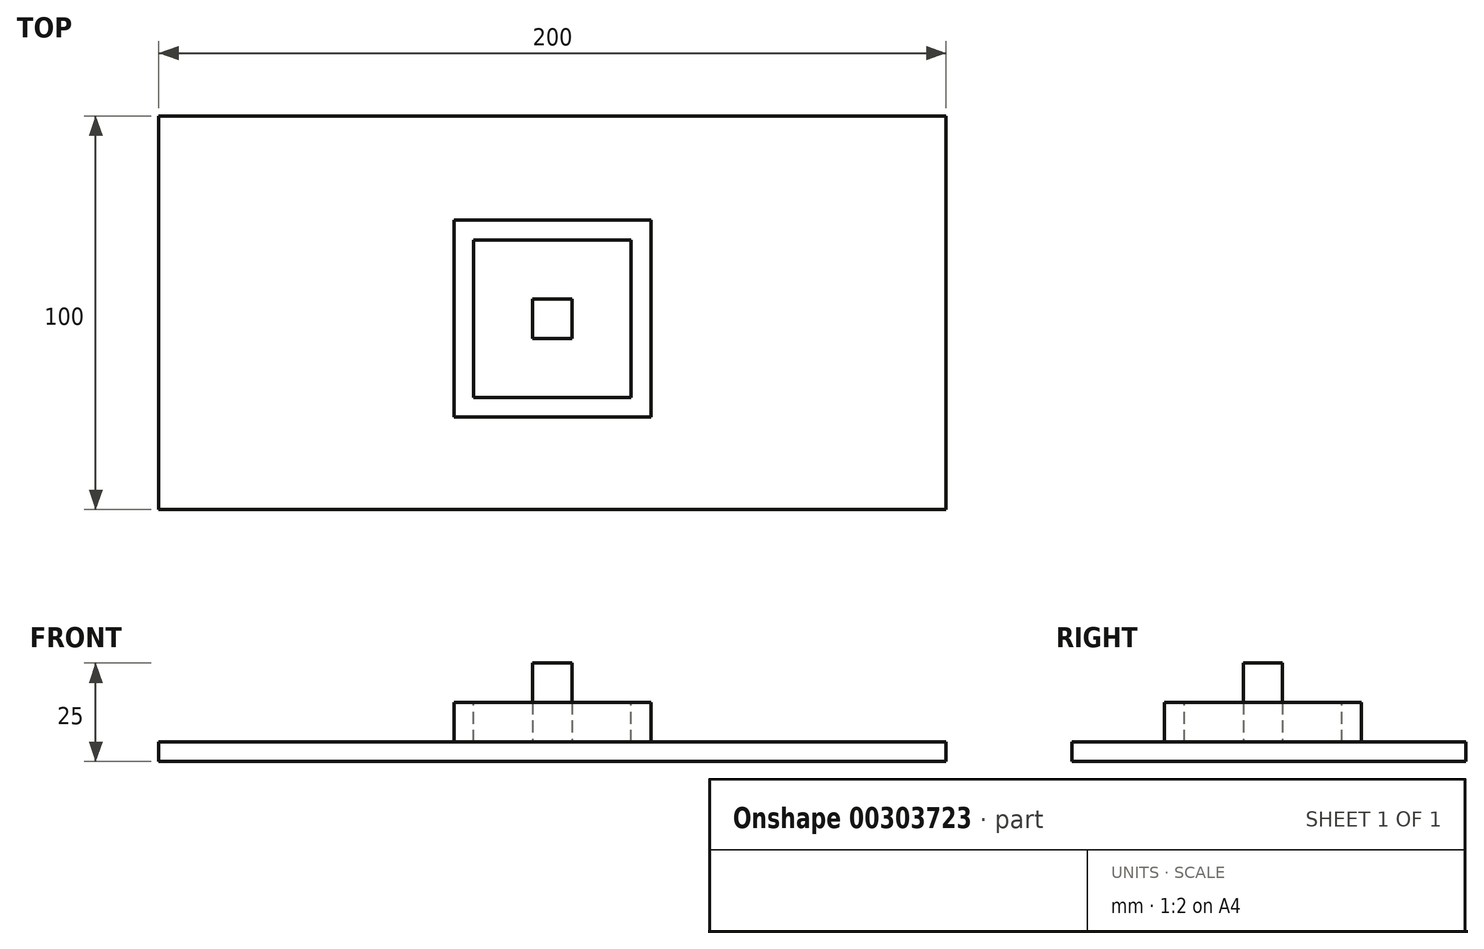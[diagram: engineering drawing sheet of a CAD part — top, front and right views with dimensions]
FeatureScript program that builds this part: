
annotation { "Feature Type Name" : "Feature", "Feature Type Description" : "" }
export const myFeature = defineFeature(function(context is Context, id is Id, definition is map)
    precondition{}
    {
        {
            var Q0;
            Q0=qCreatedBy(makeId("Top.planeOp"),FACE);
            var sketch = newSketch(context, id + "F0", { "sketchPlane" : qUnion([Q0])});
            skLineSegment(sketch, "E0.bottom", {"start": v(100, -48.5) * mm, "end": v(-100, -48.5) * mm});
            skLineSegment(sketch, "E0.top", {"start": v(100, 51.5) * mm, "end": v(-100, 51.5) * mm});
            skLineSegment(sketch, "E0.left", {"start": v(100, -48.5) * mm, "end": v(100, 51.5) * mm});
            skLineSegment(sketch, "E0.right", {"start": v(-100, -48.5) * mm, "end": v(-100, 51.5) * mm});
            skPoint(sketch, "E0.middle", {"position": v(0, 1.5) * mm});
            skSolve(sketch);
        }
        {
            var Q0;
            Q0=makeQuery(id+"F0.imprint","IMPRINT",FACE,{"disambiguationData":[TD([[makeQuery(id+"F0.imprint","IMPRINT",EDGE,{"derivedFrom":sQuery(id+"F0.wireOp",EDGE,"E0.bottom")}),-1.0]])]});
            extrude(context, id + "F1", {"entities" : qUnion([Q0]), "depth" : 5 * mm});
        }
        {
            var Q0;
            Q0=makeQuery(id+"F1.opExtrude","CAP_FACE",FACE,{"disambiguationData":[OSD([sQuery(id+"F0.wireOp",EDGE,"E0.bottom"),sQuery(id+"F0.wireOp",EDGE,"E0.top"),sQuery(id+"F0.wireOp",EDGE,"E0.left"),sQuery(id+"F0.wireOp",EDGE,"E0.right")])],"isStart":false});
            var sketch = newSketch(context, id + "F2", { "sketchPlane" : qUnion([Q0])});
            skLineSegment(sketch, "E1.bottom", {"start": v(25, -25) * mm, "end": v(-25, -25) * mm});
            skLineSegment(sketch, "E1.top", {"start": v(25, 25) * mm, "end": v(-25, 25) * mm});
            skLineSegment(sketch, "E1.left", {"start": v(25, -25) * mm, "end": v(25, 25) * mm});
            skLineSegment(sketch, "E1.right", {"start": v(-25, -25) * mm, "end": v(-25, 25) * mm});
            skPoint(sketch, "E1.middle", {"position": v(0, 0) * mm});
            skSolve(sketch);
        }
        {
            var Q0;
            Q0=makeQuery(id+"F2.imprint","IMPRINT",FACE,{"disambiguationData":[TD([[makeQuery(id+"F2.imprint","IMPRINT",EDGE,{"derivedFrom":sQuery(id+"F2.wireOp",EDGE,"E1.bottom")}),-1.0]])]});
            extrude(context, id + "F3", {"entities" : qUnion([Q0]), "operationType" : NewBodyOperationType.ADD, "depth" : 10 * mm});
        }
        {
            var Q0;
            Q0=makeQuery(id+"F3.opExtrude","CAP_FACE",FACE,{"disambiguationData":[OSD([sQuery(id+"F2.wireOp",EDGE,"E1.bottom"),sQuery(id+"F2.wireOp",EDGE,"E1.top"),sQuery(id+"F2.wireOp",EDGE,"E1.left"),sQuery(id+"F2.wireOp",EDGE,"E1.right")])],"isStart":false});
            var sketch = newSketch(context, id + "F4", { "sketchPlane" : qUnion([Q0])});
            skLineSegment(sketch, "E2.bottom", {"start": v(20, -20) * mm, "end": v(-20, -20) * mm});
            skLineSegment(sketch, "E2.top", {"start": v(20, 20) * mm, "end": v(-20, 20) * mm});
            skLineSegment(sketch, "E2.left", {"start": v(20, -20) * mm, "end": v(20, 20) * mm});
            skLineSegment(sketch, "E2.right", {"start": v(-20, -20) * mm, "end": v(-20, 20) * mm});
            skPoint(sketch, "E2.middle", {"position": v(0, 0) * mm});
            skSolve(sketch);
        }
        {
            var Q0;
            Q0=makeQuery(id+"F4.imprint","IMPRINT",FACE,{"disambiguationData":[TD([[makeQuery(id+"F4.imprint","IMPRINT",EDGE,{"derivedFrom":sQuery(id+"F4.wireOp",EDGE,"E2.bottom")}),-1.0]])]});
            extrude(context, id + "F5", {"entities" : qUnion([Q0]), "operationType" : NewBodyOperationType.REMOVE, "oppositeDirection" : true, "depth" : 10 * mm});
        }
        {
            var Q0;
            Q0=makeQuery(id+"F5.boolean.opBoolean","COPY",FACE,{"derivedFrom":makeQuery(id+"F5.opExtrude","CAP_FACE",FACE,{"disambiguationData":[OSD([sQuery(id+"F4.wireOp",EDGE,"E2.bottom"),sQuery(id+"F4.wireOp",EDGE,"E2.top"),sQuery(id+"F4.wireOp",EDGE,"E2.left"),sQuery(id+"F4.wireOp",EDGE,"E2.right")])],"isStart":false})});
            var sketch = newSketch(context, id + "F6", { "sketchPlane" : qUnion([Q0])});
            skLineSegment(sketch, "E3.bottom", {"start": v(5, -5) * mm, "end": v(-5, -5) * mm});
            skLineSegment(sketch, "E3.top", {"start": v(5, 5) * mm, "end": v(-5, 5) * mm});
            skLineSegment(sketch, "E3.left", {"start": v(5, -5) * mm, "end": v(5, 5) * mm});
            skLineSegment(sketch, "E3.right", {"start": v(-5, -5) * mm, "end": v(-5, 5) * mm});
            skPoint(sketch, "E3.middle", {"position": v(0, 0) * mm});
            skSolve(sketch);
        }
        {
            var Q0;
            Q0=makeQuery(id+"F6.imprint","IMPRINT",FACE,{"disambiguationData":[TD([[makeQuery(id+"F6.imprint","IMPRINT",EDGE,{"derivedFrom":sQuery(id+"F6.wireOp",EDGE,"E3.bottom")}),-1.0]])]});
            extrude(context, id + "F7", {"entities" : qUnion([Q0]), "operationType" : NewBodyOperationType.ADD, "depth" : 20 * mm});
        }
    });
